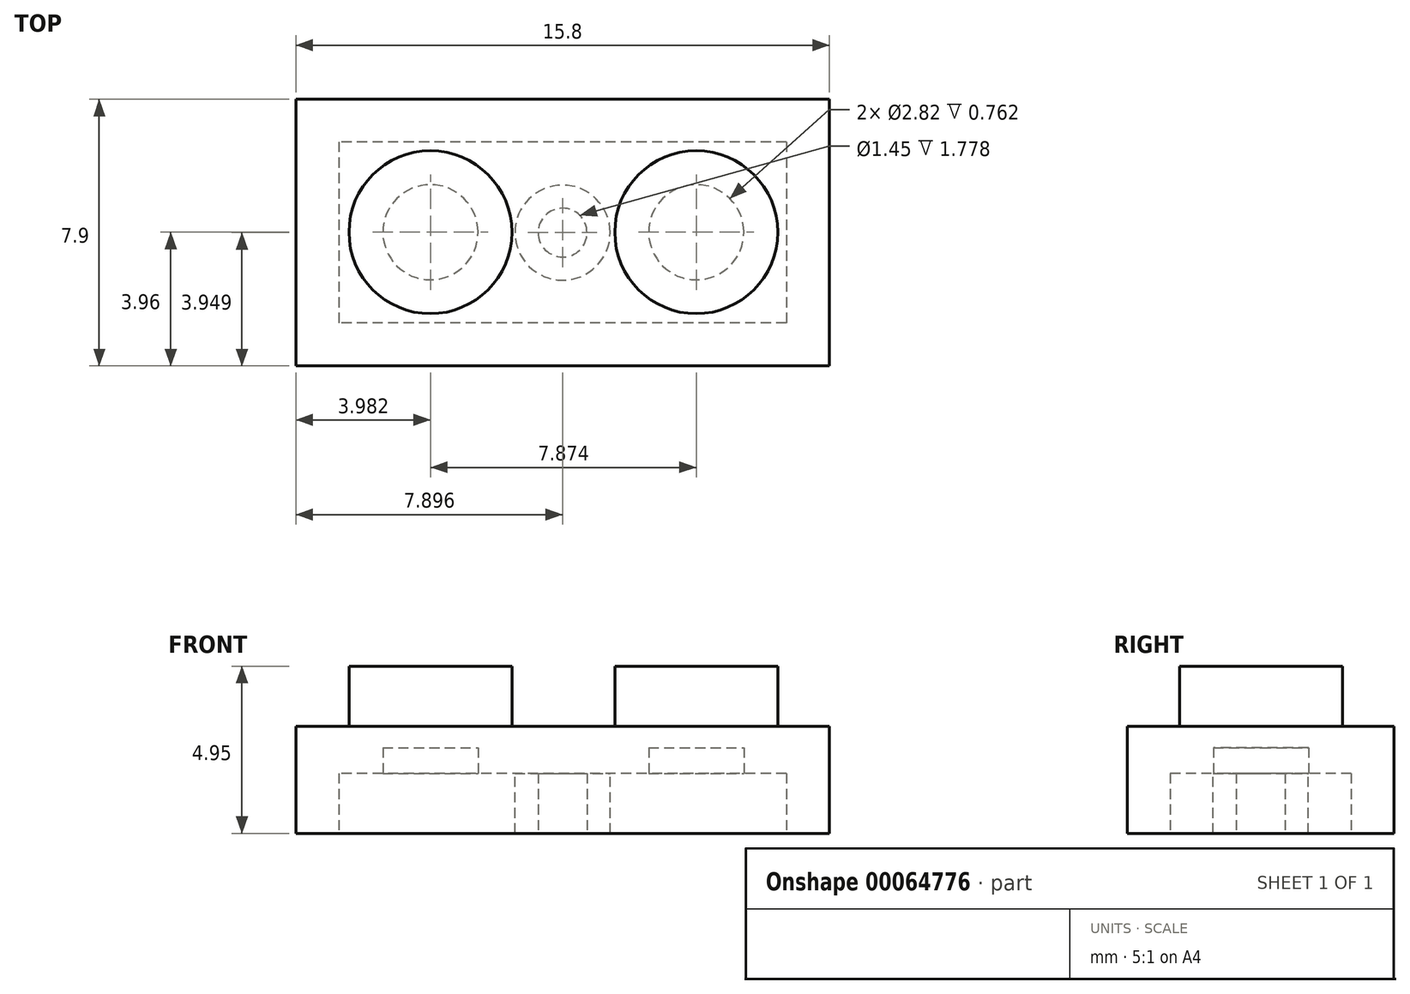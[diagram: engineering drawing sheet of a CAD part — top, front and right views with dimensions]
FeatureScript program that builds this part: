
annotation { "Feature Type Name" : "Feature", "Feature Type Description" : "" }
export const myFeature = defineFeature(function(context is Context, id is Id, definition is map)
    precondition{}
    {
        {
            var Q0;
            Q0=qCreatedBy(makeId("Top.planeOp"),FACE);
            var sketch = newSketch(context, id + "F0", { "sketchPlane" : qUnion([Q0])});
            skLineSegment(sketch, "E0.bottom", {"start": v(-52.68, 11.48) * mm, "end": v(-36.88, 11.48) * mm});
            skLineSegment(sketch, "E0.top", {"start": v(-52.68, 3.58) * mm, "end": v(-36.88, 3.58) * mm});
            skLineSegment(sketch, "E0.left", {"start": v(-52.68, 11.48) * mm, "end": v(-52.68, 3.58) * mm});
            skLineSegment(sketch, "E0.right", {"start": v(-36.88, 11.48) * mm, "end": v(-36.88, 3.58) * mm});
            skSolve(sketch);
        }
        {
            var Q0;
            Q0 = qSketchRegion(id + "F0", true);
            extrude(context, id + "F1", {"entities" : qUnion([Q0]), "depth" : 3.17 * mm});
        }
        {
            var Q0;
            Q0=makeQuery(id+"F1.opExtrude","CAP_FACE",FACE,{"disambiguationData":[OSD([sQuery(id+"F0.wireOp",EDGE,"E0.bottom"),sQuery(id+"F0.wireOp",EDGE,"E0.top"),sQuery(id+"F0.wireOp",EDGE,"E0.left"),sQuery(id+"F0.wireOp",EDGE,"E0.right")])],"isStart":false});
            var sketch = newSketch(context, id + "F2", { "sketchPlane" : qUnion([Q0])});
            skSolve(sketch);
        }
        {
            var Q0;
            Q0=makeQuery(id+"F2.imprint","IMPRINT",FACE,{"disambiguationData":[TD([[makeQuery(id+"F2.imprint","IMPRINT",EDGE,{"derivedFrom":makeQuery(id+"F1.opExtrude","CAP_EDGE",EDGE,{"disambiguationData":[OSD([sQuery(id+"F0.wireOp",EDGE,"E0.bottom")])],"isStart":false})}),-1.0]])]});
            var sketch = newSketch(context, id + "F3", { "sketchPlane" : qUnion([Q0])});
            skLineSegment(sketch, "E1", {"start": v(-40.82, 11.48) * mm, "end": v(-40.82, 7.55) * mm});
            skLineSegment(sketch, "E2", {"start": v(-36.89, 7.54) * mm, "end": v(-40.82, 7.54) * mm});
            skSolve(sketch);
        }
        {
            var Q0;
            Q0=makeQuery(id+"F3.imprint","IMPRINT",FACE,{"disambiguationData":[TD([[makeQuery(id+"F3.imprint","IMPRINT",EDGE,{"derivedFrom":makeQuery(id+"F2.imprint","IMPRINT",EDGE,{"derivedFrom":makeQuery(id+"F1.opExtrude","CAP_EDGE",EDGE,{"disambiguationData":[OSD([sQuery(id+"F0.wireOp",EDGE,"E0.bottom")])],"isStart":false})})}),-1.0]])]});
            var sketch = newSketch(context, id + "F4", { "sketchPlane" : qUnion([Q0])});
            skCircle(sketch, "E3", {"center": v(-40.82, 7.54) * mm, "radius": 2.41 * mm});
            skCircle(sketch, "E4.1.0.0", {"center": v(-48.7, 7.54) * mm, "radius": 2.41 * mm});
            skLineSegment(sketch, "E4.direction1", {"start": v(-40.82, 7.54) * mm, "end": v(-48.7, 7.54) * mm, "construction": true});
            skSolve(sketch);
        }
        {
            var Q0;
            Q0=makeQuery(id+"F4.imprint","IMPRINT",FACE,{"disambiguationData":[TD([[makeQuery(id+"F4.imprint","IMPRINT",EDGE,{"derivedFrom":sQuery(id+"F4.wireOp",EDGE,"E3")}),-1.0]])]});
            var sketch = newSketch(context, id + "F5", { "sketchPlane" : qUnion([Q0])});
            skSolve(sketch);
        }
        {
            var Q0;
            Q0 = qSketchRegion(id + "F5", true);
            var Q1;
            Q1=makeQuery(id+"F5.imprint","IMPRINT",FACE,{"disambiguationData":[TD([[makeQuery(id+"F5.imprint","IMPRINT",EDGE,{"derivedFrom":makeQuery(id+"F4.imprint","IMPRINT",EDGE,{"derivedFrom":sQuery(id+"F4.wireOp",EDGE,"E3")})}),1.0]])]});
            var Q2;
            Q2=makeQuery(id+"F5.imprint","IMPRINT",FACE,{"disambiguationData":[TD([[makeQuery(id+"F5.imprint","IMPRINT",EDGE,{"derivedFrom":makeQuery(id+"F4.imprint","IMPRINT",EDGE,{"derivedFrom":sQuery(id+"F4.wireOp",EDGE,"E4.1.0.0")})}),1.0]])]});
            extrude(context, id + "F6", {"entities" : qUnion([Q0, Q1, Q2]), "operationType" : NewBodyOperationType.ADD, "depth" : 1.78 * mm});
        }
        {
            var Q0;
            Q0=makeQuery(id+"F1.opExtrude","CAP_FACE",FACE,{"disambiguationData":[OSD([sQuery(id+"F0.wireOp",EDGE,"E0.bottom"),sQuery(id+"F0.wireOp",EDGE,"E0.top"),sQuery(id+"F0.wireOp",EDGE,"E0.left"),sQuery(id+"F0.wireOp",EDGE,"E0.right")])],"isStart":true});
            var sketch = newSketch(context, id + "F7", { "sketchPlane" : qUnion([Q0])});
            skLineSegment(sketch, "E5.rect.bottom", {"start": v(-38.15, -10.21) * mm, "end": v(-51.41, -10.21) * mm});
            skLineSegment(sketch, "E5.rect.top", {"start": v(-38.15, -4.86) * mm, "end": v(-51.41, -4.86) * mm});
            skLineSegment(sketch, "E5.rect.left", {"start": v(-38.15, -10.21) * mm, "end": v(-38.15, -4.86) * mm});
            skLineSegment(sketch, "E5.rect.right", {"start": v(-51.41, -10.21) * mm, "end": v(-51.41, -4.86) * mm});
            skPoint(sketch, "E5.rect.middle", {"position": v(-44.78, -7.54) * mm});
            skLineSegment(sketch, "E6", {"start": v(-36.88, -7.53) * mm, "end": v(-38.15, -7.53) * mm});
            skLineSegment(sketch, "E7", {"start": v(-44.42, -3.58) * mm, "end": v(-44.42, -4.85) * mm});
            skLineSegment(sketch, "E8", {"start": v(-44.3, -11.48) * mm, "end": v(-44.3, -10.21) * mm});
            skSolve(sketch);
        }
        {
            var Q0;
            {var subQ4=sQuery(id+"F7.wireOp",EDGE,"E5.rect.top");Q0=makeQuery(id+"F7.imprint","IMPRINT",FACE,{"disambiguationData":[TD([[makeQuery(id+"F7.imprint","IMPRINT",EDGE,{"derivedFrom":subQ4}),1.0]])]});}
            extrude(context, id + "F8", {"entities" : qUnion([Q0]), "operationType" : NewBodyOperationType.REMOVE, "oppositeDirection" : true, "depth" : 1.78 * mm});
        }
        {
            var Q0;
            Q0=makeQuery(id+"F8.boolean.opBoolean","COPY",FACE,{"derivedFrom":makeQuery(id+"F8.opExtrude","CAP_FACE",FACE,{"disambiguationData":[OSD([sQuery(id+"F7.wireOp",EDGE,"E5.rect.bottom"),sQuery(id+"F7.wireOp",EDGE,"E5.rect.top"),sQuery(id+"F7.wireOp",EDGE,"E5.rect.left"),sQuery(id+"F7.wireOp",EDGE,"E5.rect.right")])],"isStart":false})});
            var sketch = newSketch(context, id + "F9", { "sketchPlane" : qUnion([Q0])});
            skLineSegment(sketch, "E9", {"start": v(-36.88, -7.53) * mm, "end": v(-44.78, -7.53) * mm});
            skCircle(sketch, "E10", {"center": v(-44.78, -7.53) * mm, "radius": 1.4 * mm});
            skSolve(sketch);
        }
        {
            var Q0;
            Q0 = qSketchRegion(id + "F9", true);
            extrude(context, id + "F10", {"entities" : qUnion([Q0]), "operationType" : NewBodyOperationType.ADD, "depth" : 1.78 * mm});
        }
        {
            var Q0;
            Q0=makeQuery(id+"F8.boolean.opBoolean","COPY",FACE,{"derivedFrom":makeQuery(id+"F8.opExtrude","CAP_FACE",FACE,{"disambiguationData":[OSD([sQuery(id+"F7.wireOp",EDGE,"E5.rect.bottom"),sQuery(id+"F7.wireOp",EDGE,"E5.rect.top"),sQuery(id+"F7.wireOp",EDGE,"E5.rect.left"),sQuery(id+"F7.wireOp",EDGE,"E5.rect.right")])],"isStart":false})});
            var sketch = newSketch(context, id + "F11", { "sketchPlane" : qUnion([Q0])});
            skCircle(sketch, "E11", {"center": v(-40.82, -7.54) * mm, "radius": 1.4 * mm});
            skCircle(sketch, "E12.1.0.0", {"center": v(-48.7, -7.54) * mm, "radius": 1.4 * mm});
            skLineSegment(sketch, "E12.direction1", {"start": v(-40.82, -7.54) * mm, "end": v(-48.7, -7.54) * mm, "construction": true});
            skSolve(sketch);
        }
        {
            var Q0;
            Q0=makeQuery(id+"F11.imprint","IMPRINT",FACE,{"disambiguationData":[TD([[makeQuery(id+"F11.imprint","IMPRINT",EDGE,{"derivedFrom":sQuery(id+"F11.wireOp",EDGE,"E11")}),1.0]])]});
            var Q1;
            Q1=makeQuery(id+"F11.imprint","IMPRINT",FACE,{"disambiguationData":[TD([[makeQuery(id+"F11.imprint","IMPRINT",EDGE,{"derivedFrom":sQuery(id+"F11.wireOp",EDGE,"E12.1.0.0")}),1.0]])]});
            extrude(context, id + "F12", {"entities" : qUnion([Q0, Q1]), "operationType" : NewBodyOperationType.REMOVE, "oppositeDirection" : true, "depth" : 0.76 * mm});
        }
        {
            var Q0;
            Q0=makeQuery(id+"F10.opExtrude","CAP_FACE",FACE,{"disambiguationData":[OSD([sQuery(id+"F9.wireOp",EDGE,"E10")])],"isStart":false});
            var sketch = newSketch(context, id + "F13", { "sketchPlane" : qUnion([Q0])});
            skCircle(sketch, "E13", {"center": v(-44.78, -7.53) * mm, "radius": 0.72 * mm});
            skSolve(sketch);
        }
        {
            var Q0;
            Q0=makeQuery(id+"F13.imprint","IMPRINT",FACE,{"disambiguationData":[TD([[makeQuery(id+"F13.imprint","IMPRINT",EDGE,{"derivedFrom":sQuery(id+"F13.wireOp",EDGE,"E13")}),1.0]])]});
            extrude(context, id + "F14", {"entities" : qUnion([Q0]), "operationType" : NewBodyOperationType.REMOVE, "oppositeDirection" : true, "depth" : 1.78 * mm});
        }
    });
